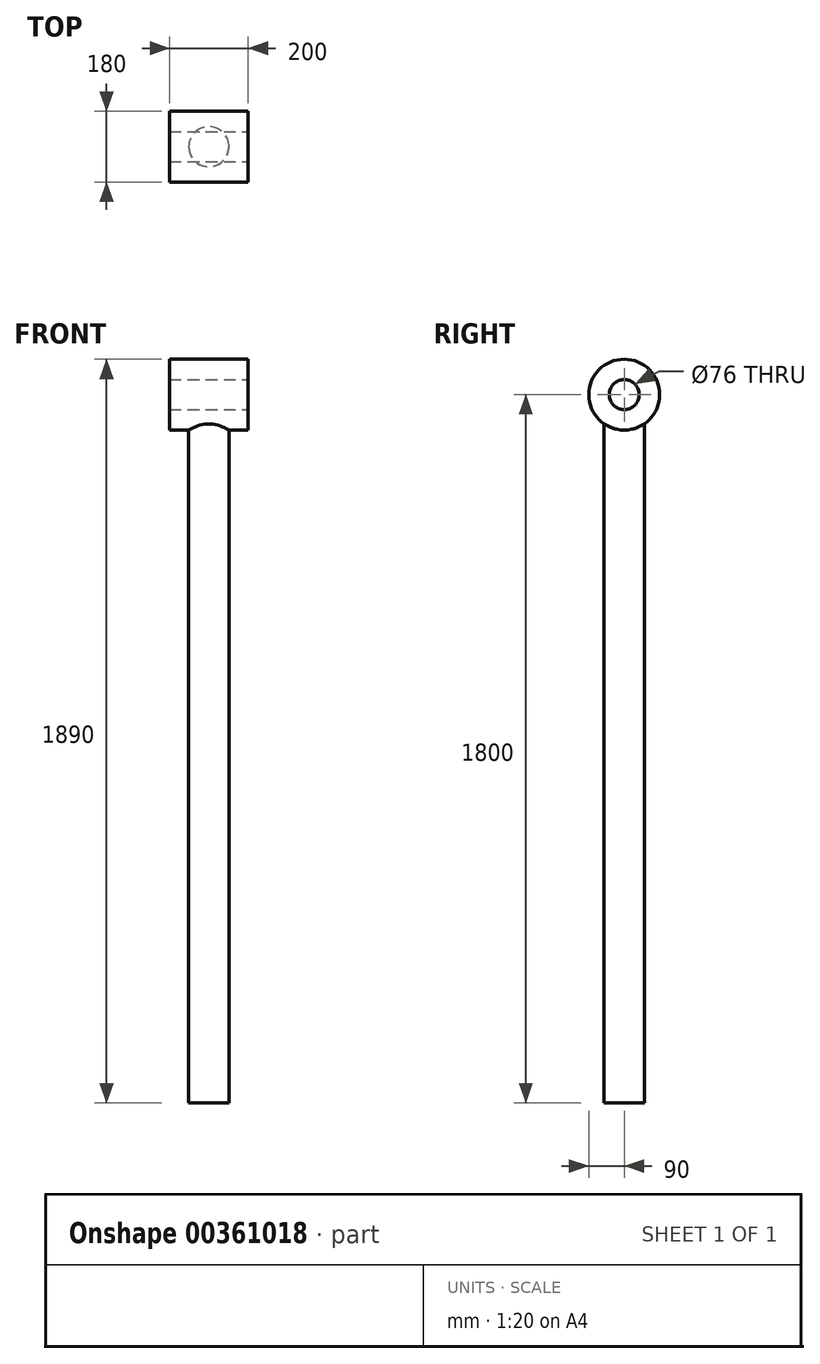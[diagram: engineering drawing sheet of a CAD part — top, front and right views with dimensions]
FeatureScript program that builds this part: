
annotation { "Feature Type Name" : "Feature", "Feature Type Description" : "" }
export const myFeature = defineFeature(function(context is Context, id is Id, definition is map)
    precondition{}
    {
        {
            var Q0;
            Q0=qCreatedBy(makeId("Top.planeOp"),FACE);
            var sketch = newSketch(context, id + "F0", { "sketchPlane" : qUnion([Q0])});
            skCircle(sketch, "E0", {"center": v(0, 0) * mm, "radius": 51 * mm});
            skSolve(sketch);
        }
        {
            var Q0;
            Q0=makeQuery(id+"F0.imprint","IMPRINT",FACE,{"disambiguationData":[TD([[makeQuery(id+"F0.imprint","IMPRINT",EDGE,{"derivedFrom":sQuery(id+"F0.wireOp",EDGE,"E0")}),1.0]])]});
            extrude(context, id + "F1", {"entities" : qUnion([Q0]), "depth" : 1800 * mm});
        }
        {
            var Q0;
            Q0=qCreatedBy(makeId("Right.planeOp"),FACE);
            var sketch = newSketch(context, id + "F2", { "sketchPlane" : qUnion([Q0])});
            skCircle(sketch, "E1", {"center": v(0, 1800) * mm, "radius": 90 * mm});
            skSolve(sketch);
        }
        {
            var Q0;
            Q0 = qSketchRegion(id + "F2", true);
            extrude(context, id + "F3", {"entities" : qUnion([Q0]), "operationType" : NewBodyOperationType.ADD, "endBound" : BoundingType.SYMMETRIC, "depth" : 200 * mm});
        }
        {
            var Q0;
            Q0=makeQuery(id+"F3.opExtrude","CAP_FACE",FACE,{"disambiguationData":[OSD([sQuery(id+"F2.wireOp",EDGE,"E1")])],"isStart":false});
            var sketch = newSketch(context, id + "F4", { "sketchPlane" : qUnion([Q0])});
            skCircle(sketch, "E2", {"center": v(0, 1800) * mm, "radius": 38 * mm});
            skSolve(sketch);
        }
        {
            var Q0;
            Q0=makeQuery(id+"F4.imprint","IMPRINT",FACE,{"disambiguationData":[TD([[makeQuery(id+"F4.imprint","IMPRINT",EDGE,{"derivedFrom":sQuery(id+"F4.wireOp",EDGE,"E2")}),1.0]])]});
            extrude(context, id + "F5", {"entities" : qUnion([Q0]), "operationType" : NewBodyOperationType.REMOVE, "endBound" : BoundingType.THROUGH_ALL, "oppositeDirection" : true, "depth" : 25 * mm});
        }
    });
